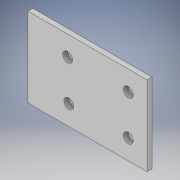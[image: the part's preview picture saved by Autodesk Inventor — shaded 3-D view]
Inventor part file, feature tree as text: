
AUTODESK INVENTOR PART (.ipt)
format: ipt  version: 2017 (Build 210142000, 142)  size: 105,472 bytes
history: native  units: in
note: dims shown in document units (in); Inventor stores cm internally (conversion verified against a paired STEP export)
features: extrude x1, sketch x1
ambient origin geometry x8: Origin, YZ Plane, XZ Plane, XY Plane, X Axis, Y Axis, Z Axis, Center Point
bodies: Solid1 (feature_tree)
feature tree (2):
  extrude  "Extrusion1"  Depth=2.0in
  sketch  "Sketch1"  dims[d0=3.0in d1=2.0in d2=0.25in d3=0.25in d4=1.0in d5=0.5in d6=1.0in d7=0.25in d8=0.25in d9=1.0in d10=0.125in d11=0.0in d12=0.5in]
